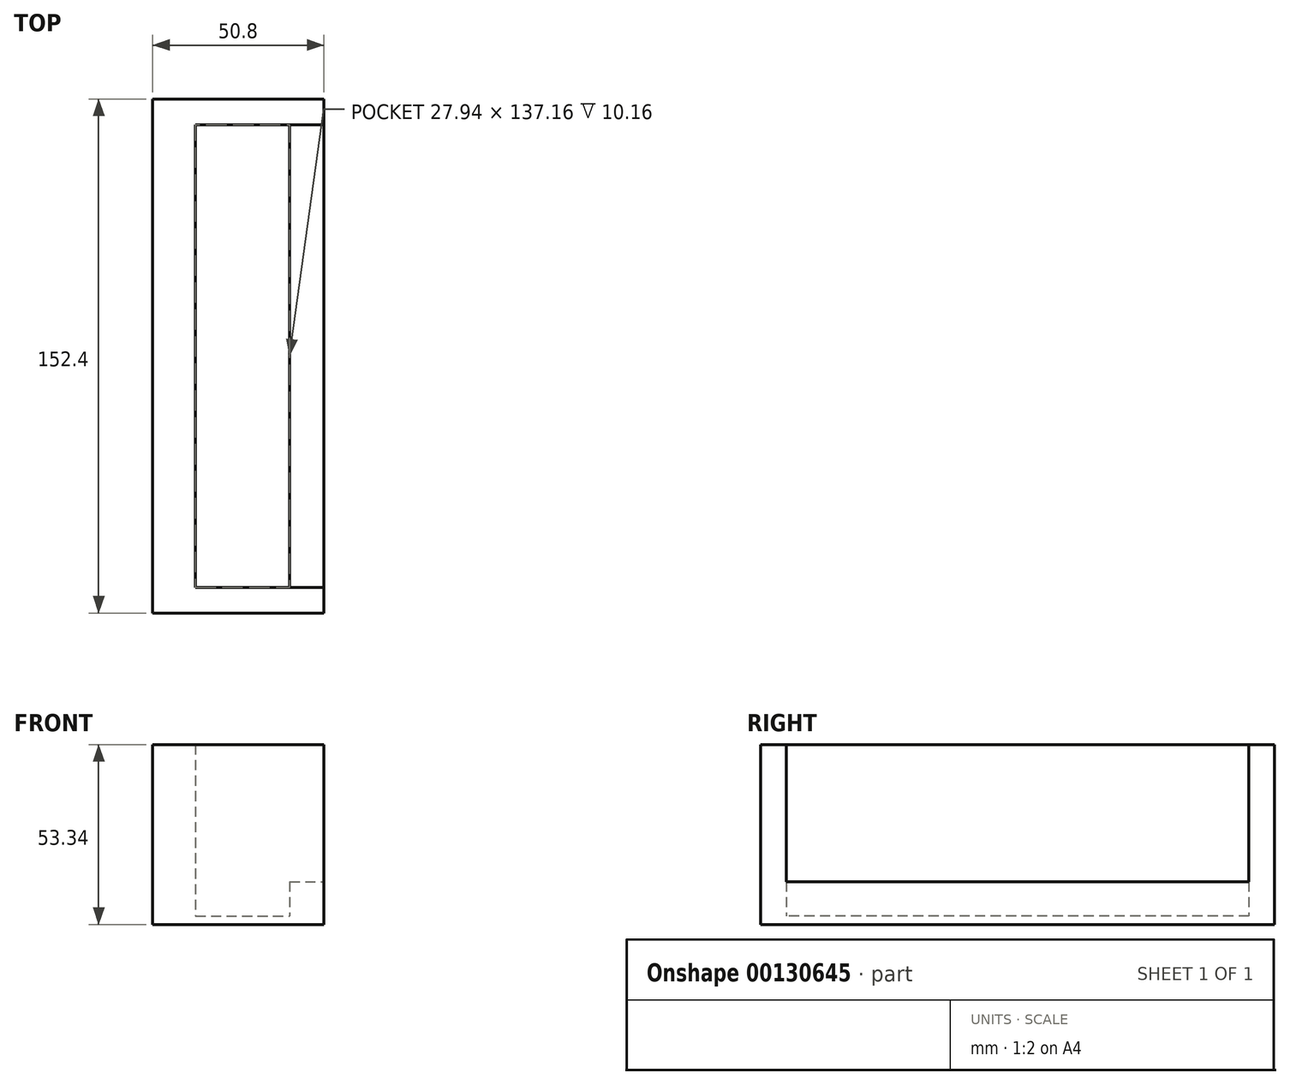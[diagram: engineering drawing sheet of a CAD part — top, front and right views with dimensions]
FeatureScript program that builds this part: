
annotation { "Feature Type Name" : "Feature", "Feature Type Description" : "" }
export const myFeature = defineFeature(function(context is Context, id is Id, definition is map)
    precondition{}
    {
        {
            var Q0;
            Q0=qCreatedBy(makeId("Front.planeOp"),FACE);
            var sketch = newSketch(context, id + "F0", { "sketchPlane" : qUnion([Q0])});
            skLineSegment(sketch, "E0.bottom", {"start": v(-62.05, 13.46) * mm, "end": v(-11.25, 13.46) * mm});
            skLineSegment(sketch, "E0.top", {"start": v(-62.05, 10.92) * mm, "end": v(-11.25, 10.92) * mm});
            skLineSegment(sketch, "E0.left", {"start": v(-62.05, 13.46) * mm, "end": v(-62.05, 10.92) * mm});
            skLineSegment(sketch, "E0.right", {"start": v(-11.25, 13.46) * mm, "end": v(-11.25, 10.92) * mm});
            skSolve(sketch);
        }
        {
            var Q0;
            Q0=makeQuery(id+"F0.imprint","IMPRINT",FACE,{"disambiguationData":[TD([[makeQuery(id+"F0.imprint","IMPRINT",EDGE,{"derivedFrom":sQuery(id+"F0.wireOp",EDGE,"E0.bottom")}),-1.0]])]});
            extrude(context, id + "F1", {"entities" : qUnion([Q0]), "depth" : 152.4 * mm});
        }
        {
            var Q0;
            Q0=makeQuery(id+"F1.opExtrude","SWEPT_FACE",FACE,{"disambiguationData":[OSD([sQuery(id+"F0.wireOp",EDGE,"E0.bottom")])]});
            var sketch = newSketch(context, id + "F2", { "sketchPlane" : qUnion([Q0])});
            skLineSegment(sketch, "E1.bottom", {"start": v(-62.05, 0) * mm, "end": v(-49.35, 0) * mm});
            skLineSegment(sketch, "E1.top", {"start": v(-62.05, -152.4) * mm, "end": v(-49.35, -152.4) * mm});
            skLineSegment(sketch, "E1.left", {"start": v(-62.05, 0) * mm, "end": v(-62.05, -152.4) * mm});
            skLineSegment(sketch, "E1.right", {"start": v(-49.35, 0) * mm, "end": v(-49.35, -152.4) * mm});
            skSolve(sketch);
        }
        {
            var Q0;
            Q0=makeQuery(id+"F2.imprint","IMPRINT",FACE,{"disambiguationData":[TD([[makeQuery(id+"F2.imprint","IMPRINT",EDGE,{"derivedFrom":sQuery(id+"F2.wireOp",EDGE,"E1.bottom")}),-1.0]])]});
            extrude(context, id + "F3", {"entities" : qUnion([Q0]), "operationType" : NewBodyOperationType.ADD, "depth" : 50.8 * mm});
        }
        {
            var Q0;
            Q0=makeQuery(id+"F1.opExtrude","SWEPT_FACE",FACE,{"disambiguationData":[OSD([sQuery(id+"F0.wireOp",EDGE,"E0.bottom")])]});
            var sketch = newSketch(context, id + "F4", { "sketchPlane" : qUnion([Q0])});
            skLineSegment(sketch, "E2.bottom", {"start": v(-49.35, -152.4) * mm, "end": v(-11.25, -152.4) * mm});
            skLineSegment(sketch, "E2.top", {"start": v(-49.35, -144.78) * mm, "end": v(-11.25, -144.78) * mm});
            skLineSegment(sketch, "E2.left", {"start": v(-49.35, -152.4) * mm, "end": v(-49.35, -144.78) * mm});
            skLineSegment(sketch, "E2.right", {"start": v(-11.25, -152.4) * mm, "end": v(-11.25, -144.78) * mm});
            skLineSegment(sketch, "E3.bottom", {"start": v(-49.35, 0) * mm, "end": v(-11.25, 0) * mm});
            skLineSegment(sketch, "E3.top", {"start": v(-49.35, -7.62) * mm, "end": v(-11.25, -7.62) * mm});
            skLineSegment(sketch, "E3.left", {"start": v(-49.35, 0) * mm, "end": v(-49.35, -7.62) * mm});
            skLineSegment(sketch, "E3.right", {"start": v(-11.25, 0) * mm, "end": v(-11.25, -7.62) * mm});
            skSolve(sketch);
        }
        {
            var Q0;
            Q0=makeQuery(id+"F4.imprint","IMPRINT",FACE,{"disambiguationData":[TD([[makeQuery(id+"F4.imprint","IMPRINT",EDGE,{"derivedFrom":sQuery(id+"F4.wireOp",EDGE,"E2.bottom")}),1.0]])]});
            extrude(context, id + "F5", {"entities" : qUnion([Q0]), "operationType" : NewBodyOperationType.ADD, "depth" : 50.8 * mm});
        }
        {
            var Q0;
            Q0=makeQuery(id+"F4.imprint","IMPRINT",FACE,{"disambiguationData":[TD([[makeQuery(id+"F4.imprint","IMPRINT",EDGE,{"derivedFrom":sQuery(id+"F4.wireOp",EDGE,"E3.bottom")}),-1.0]])]});
            extrude(context, id + "F6", {"entities" : qUnion([Q0]), "operationType" : NewBodyOperationType.ADD, "depth" : 50.8 * mm});
        }
        {
            var Q0;
            Q0=makeQuery(id+"F1.opExtrude","SWEPT_FACE",FACE,{"disambiguationData":[OSD([sQuery(id+"F0.wireOp",EDGE,"E0.bottom")])]});
            var sketch = newSketch(context, id + "F7", { "sketchPlane" : qUnion([Q0])});
            skLineSegment(sketch, "E4.bottom", {"start": v(-11.25, -7.62) * mm, "end": v(-21.41, -7.62) * mm});
            skLineSegment(sketch, "E4.top", {"start": v(-11.25, -144.78) * mm, "end": v(-21.41, -144.78) * mm});
            skLineSegment(sketch, "E4.left", {"start": v(-11.25, -7.62) * mm, "end": v(-11.25, -144.78) * mm});
            skLineSegment(sketch, "E4.right", {"start": v(-21.41, -7.62) * mm, "end": v(-21.41, -144.78) * mm});
            skSolve(sketch);
        }
        {
            var Q0;
            Q0 = qSketchRegion(id + "F7", true);
            extrude(context, id + "F8", {"entities" : qUnion([Q0]), "operationType" : NewBodyOperationType.ADD, "depth" : 10.16 * mm});
        }
    });
